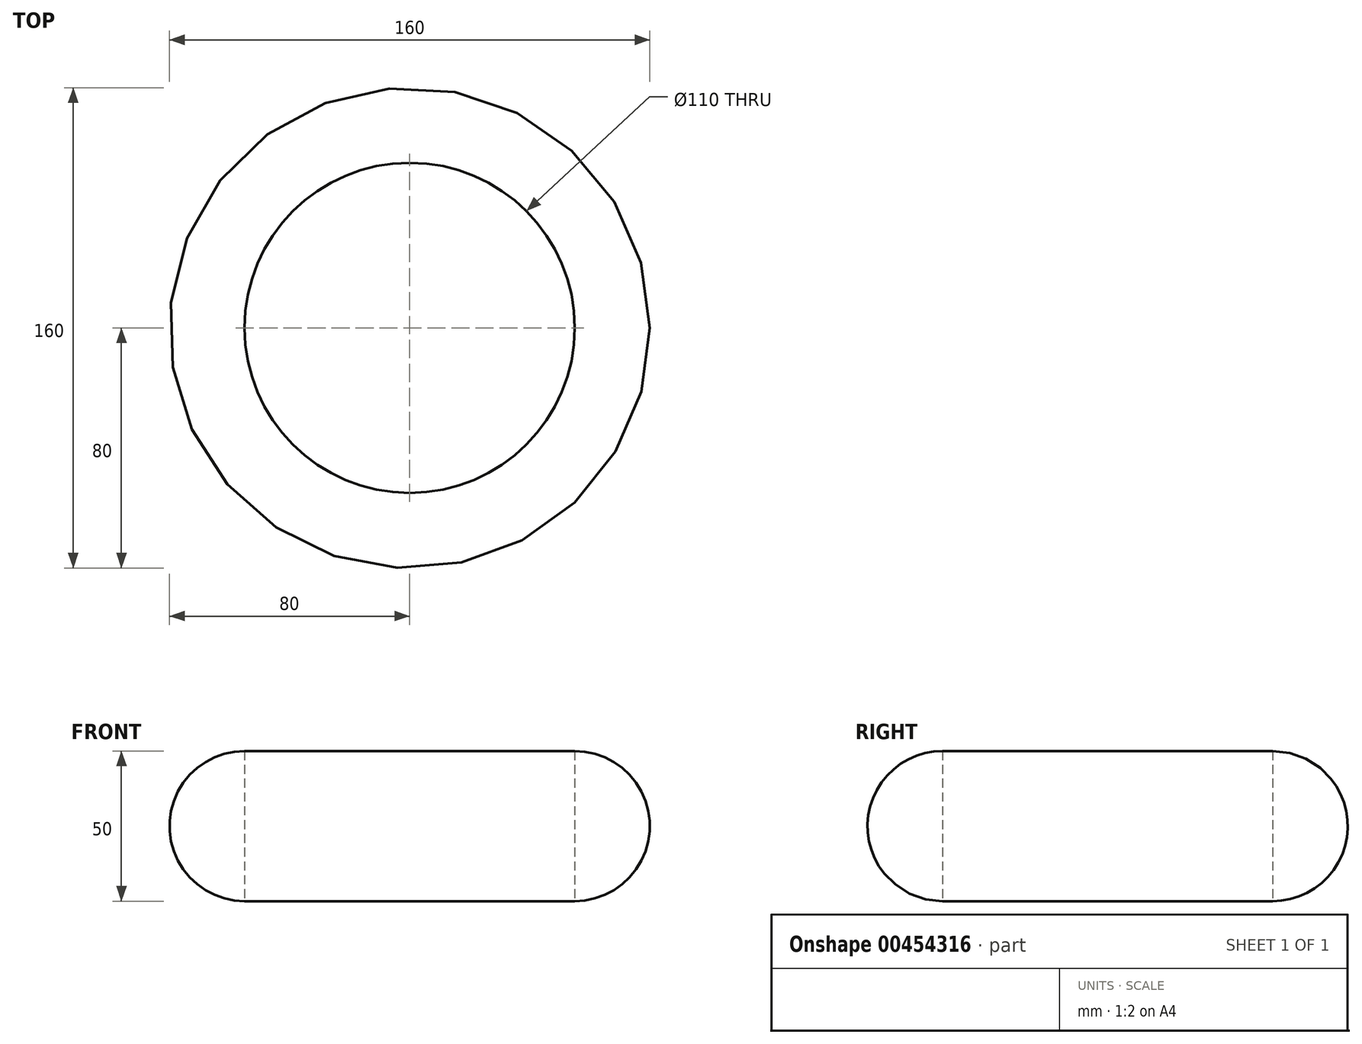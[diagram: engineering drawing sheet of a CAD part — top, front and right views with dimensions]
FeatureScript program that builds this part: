
annotation { "Feature Type Name" : "Feature", "Feature Type Description" : "" }
export const myFeature = defineFeature(function(context is Context, id is Id, definition is map)
    precondition{}
    {
        {
            var Q0;
            Q0=qCreatedBy(makeId("Top.planeOp"),FACE);
            var sketch = newSketch(context, id + "F0", { "sketchPlane" : qUnion([Q0])});
            skCircle(sketch, "E0", {"center": v(0, 0) * mm, "radius": 80 * mm});
            skSolve(sketch);
        }
        {
            var Q0;
            Q0 = qSketchRegion(id + "F0", true);
            extrude(context, id + "F1", {"entities" : qUnion([Q0]), "depth" : 50 * mm});
        }
        {
            var Q0;
            Q0=makeQuery(id+"F1.opExtrude","SWEPT_FACE",FACE,{"disambiguationData":[OSD([sQuery(id+"F0.wireOp",EDGE,"E0")])]});
            fillet(context, id + "F2", {"entities" : qUnion([Q0]), "radius" : 25 * mm, "tangentPropagation" : true, "allowEdgeOverflow" : false});
        }
        {
            var Q0;
            Q0=makeQuery(id+"F1.opExtrude","CAP_FACE",FACE,{"disambiguationData":[OSD([sQuery(id+"F0.wireOp",EDGE,"E0")])],"isStart":true});
            var sketch = newSketch(context, id + "F3", { "sketchPlane" : qUnion([Q0])});
            skCircle(sketch, "E1", {"center": v(0, 0) * mm, "radius": 55 * mm});
            skSolve(sketch);
        }
        {
            var Q0;
            Q0 = qSketchRegion(id + "F3", true);
            extrude(context, id + "F4", {"entities" : qUnion([Q0]), "operationType" : NewBodyOperationType.REMOVE, "oppositeDirection" : true, "depth" : 50 * mm});
        }
    });
